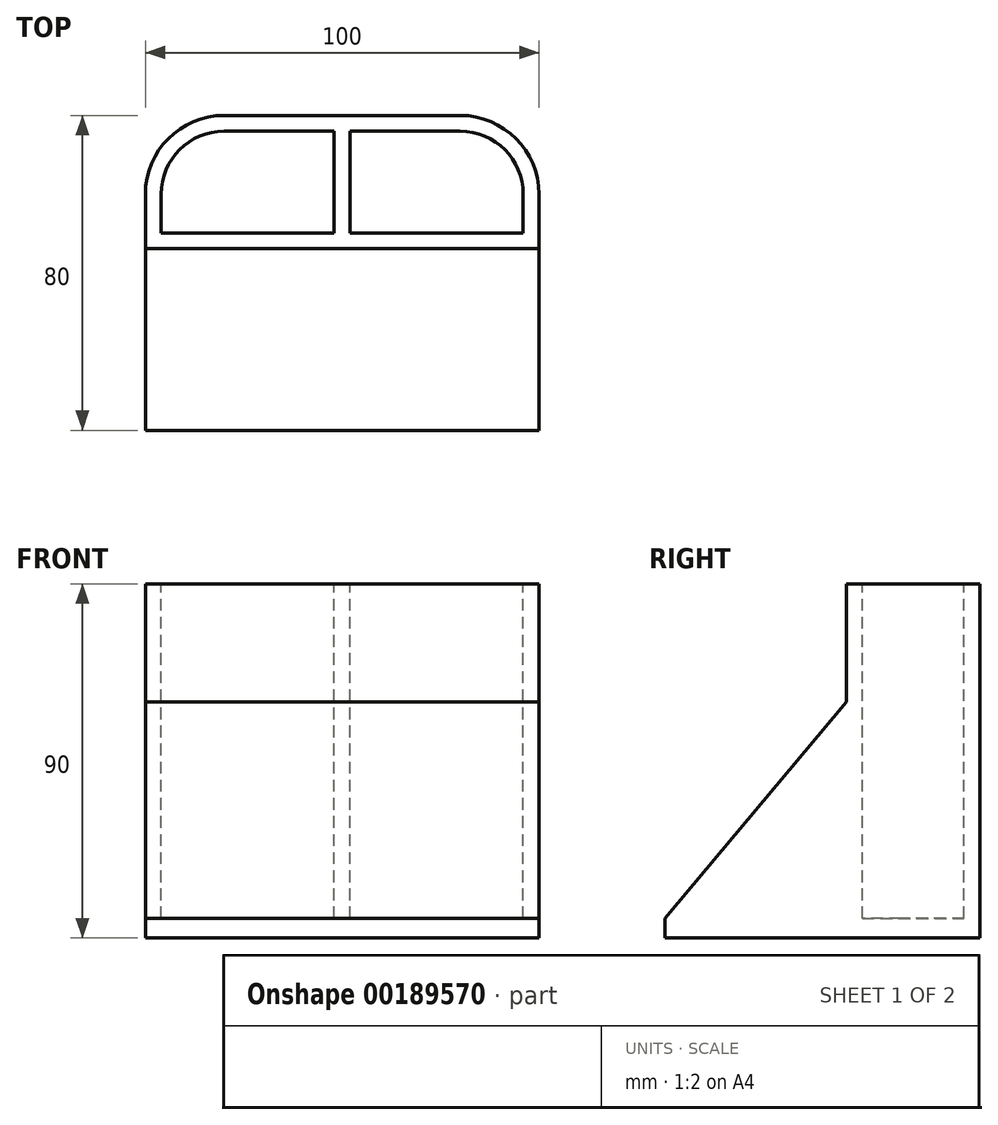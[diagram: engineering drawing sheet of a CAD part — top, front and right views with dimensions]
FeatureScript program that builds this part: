
annotation { "Feature Type Name" : "Feature", "Feature Type Description" : "" }
export const myFeature = defineFeature(function(context is Context, id is Id, definition is map)
    precondition{}
    {
        {
            var Q0;
            Q0=qCreatedBy(makeId("Top.planeOp"),FACE);
            var sketch = newSketch(context, id + "F0", { "sketchPlane" : qUnion([Q0])});
            skLineSegment(sketch, "E0.bottom", {"start": v(50, -40) * mm, "end": v(-50, -40) * mm});
            skLineSegment(sketch, "E0.top", {"start": v(30, 40) * mm, "end": v(-30, 40) * mm});
            skLineSegment(sketch, "E0.left", {"start": v(50, -40) * mm, "end": v(50, 20) * mm});
            skLineSegment(sketch, "E0.right", {"start": v(-50, -40) * mm, "end": v(-50, 20) * mm});
            skPoint(sketch, "E0.middle", {"position": v(0, 0) * mm});
            skPoint(sketch, "E1.visualSharp", {"position": v(-50, 40) * mm});
            skArc(sketch, "E1.filletArc", {"start": v(-30, 40) * mm, "mid": v(-44.14, 34.14) * mm, "end": v(-50, 20) * mm});
            skPoint(sketch, "E2.visualSharp", {"position": v(50, 40) * mm});
            skArc(sketch, "E2.filletArc", {"start": v(50, 20) * mm, "mid": v(44.14, 34.14) * mm, "end": v(30, 40) * mm});
            skSolve(sketch);
        }
        {
            var Q0;
            Q0=makeQuery(id+"F0.imprint","IMPRINT",FACE,{"disambiguationData":[TD([[makeQuery(id+"F0.imprint","IMPRINT",EDGE,{"derivedFrom":sQuery(id+"F0.wireOp",EDGE,"E0.bottom")}),-1.0]])]});
            extrude(context, id + "F1", {"entities" : qUnion([Q0]), "depth" : 60 * mm});
        }
        {
            var Q0;
            Q0=makeQuery(id+"F1.opExtrude","CAP_EDGE",EDGE,{"disambiguationData":[OSD([sQuery(id+"F0.wireOp",EDGE,"E0.bottom")])],"isStart":false});
            chamfer(context, id + "F2", {"entities" : qUnion([Q0]), "chamferType" : ChamferType.OFFSET_ANGLE, "width" : 55 * mm, "oppositeDirection" : false, "angle" : 40 * degree, "tangentPropagation" : true});
        }
        {
            var Q0;
            Q0=makeQuery(id+"F1.opExtrude","CAP_FACE",FACE,{"disambiguationData":[OSD([sQuery(id+"F0.wireOp",EDGE,"E0.bottom"),sQuery(id+"F0.wireOp",EDGE,"E0.top"),sQuery(id+"F0.wireOp",EDGE,"E0.left"),sQuery(id+"F0.wireOp",EDGE,"E0.right"),sQuery(id+"F0.wireOp",EDGE,"E1.filletArc"),sQuery(id+"F0.wireOp",EDGE,"E2.filletArc")])],"isStart":false});
            extrude(context, id + "F3", {"entities" : qUnion([Q0]), "operationType" : NewBodyOperationType.ADD, "depth" : 30 * mm});
        }
        {
            var Q0;
            Q0=makeQuery(id+"F3.opExtrude","CAP_FACE",FACE,{"disambiguationData":[OSD([sQuery(id+"F0.wireOp",EDGE,"E0.bottom"),sQuery(id+"F0.wireOp",EDGE,"E0.top"),sQuery(id+"F0.wireOp",EDGE,"E0.left"),sQuery(id+"F0.wireOp",EDGE,"E0.right"),sQuery(id+"F0.wireOp",EDGE,"E1.filletArc"),sQuery(id+"F0.wireOp",EDGE,"E2.filletArc")])],"isStart":false});
            var sketch = newSketch(context, id + "F4", { "sketchPlane" : qUnion([Q0])});
            skArc(sketch, "E3.0", {"start": v(-30, 36) * mm, "mid": v(-41.31, 31.31) * mm, "end": v(-46, 20) * mm});
            skLineSegment(sketch, "E3.1", {"start": v(-46, 10.15) * mm, "end": v(46, 10.15) * mm});
            skLineSegment(sketch, "E3.2", {"start": v(46, 10.15) * mm, "end": v(46, 20) * mm});
            skLineSegment(sketch, "E3.3", {"start": v(-46, 20) * mm, "end": v(-46, 10.15) * mm});
            skArc(sketch, "E3.4", {"start": v(46, 20) * mm, "mid": v(41.31, 31.31) * mm, "end": v(30, 36) * mm});
            skLineSegment(sketch, "E3.5", {"start": v(30, 36) * mm, "end": v(-30, 36) * mm});
            skLineSegment(sketch, "E4", {"start": v(0, 10.15) * mm, "end": v(0, 36) * mm, "construction": true});
            skLineSegment(sketch, "E5", {"start": v(-2, 10.15) * mm, "end": v(-2, 36) * mm});
            skLineSegment(sketch, "E6.MirrorCS", {"start": v(2, 10.15) * mm, "end": v(2, 36) * mm});
            skSolve(sketch);
        }
        {
            var Q0;
            {var subQ3=sQuery(id+"F4.wireOp",EDGE,"E3.2");Q0=makeQuery(id+"F4.imprint","IMPRINT",FACE,{"disambiguationData":[TD([[makeQuery(id+"F4.imprint","IMPRINT",EDGE,{"derivedFrom":subQ3}),1.0]])]});}
            var Q1;
            {var subQ1=sQuery(id+"F4.wireOp",EDGE,"E3.0");Q1=makeQuery(id+"F4.imprint","IMPRINT",FACE,{"disambiguationData":[TD([[makeQuery(id+"F4.imprint","IMPRINT",EDGE,{"derivedFrom":subQ1}),1.0]])]});}
            extrude(context, id + "F5", {"entities" : qUnion([Q0, Q1]), "operationType" : NewBodyOperationType.REMOVE, "oppositeDirection" : true, "depth" : 85 * mm});
        }
    });
